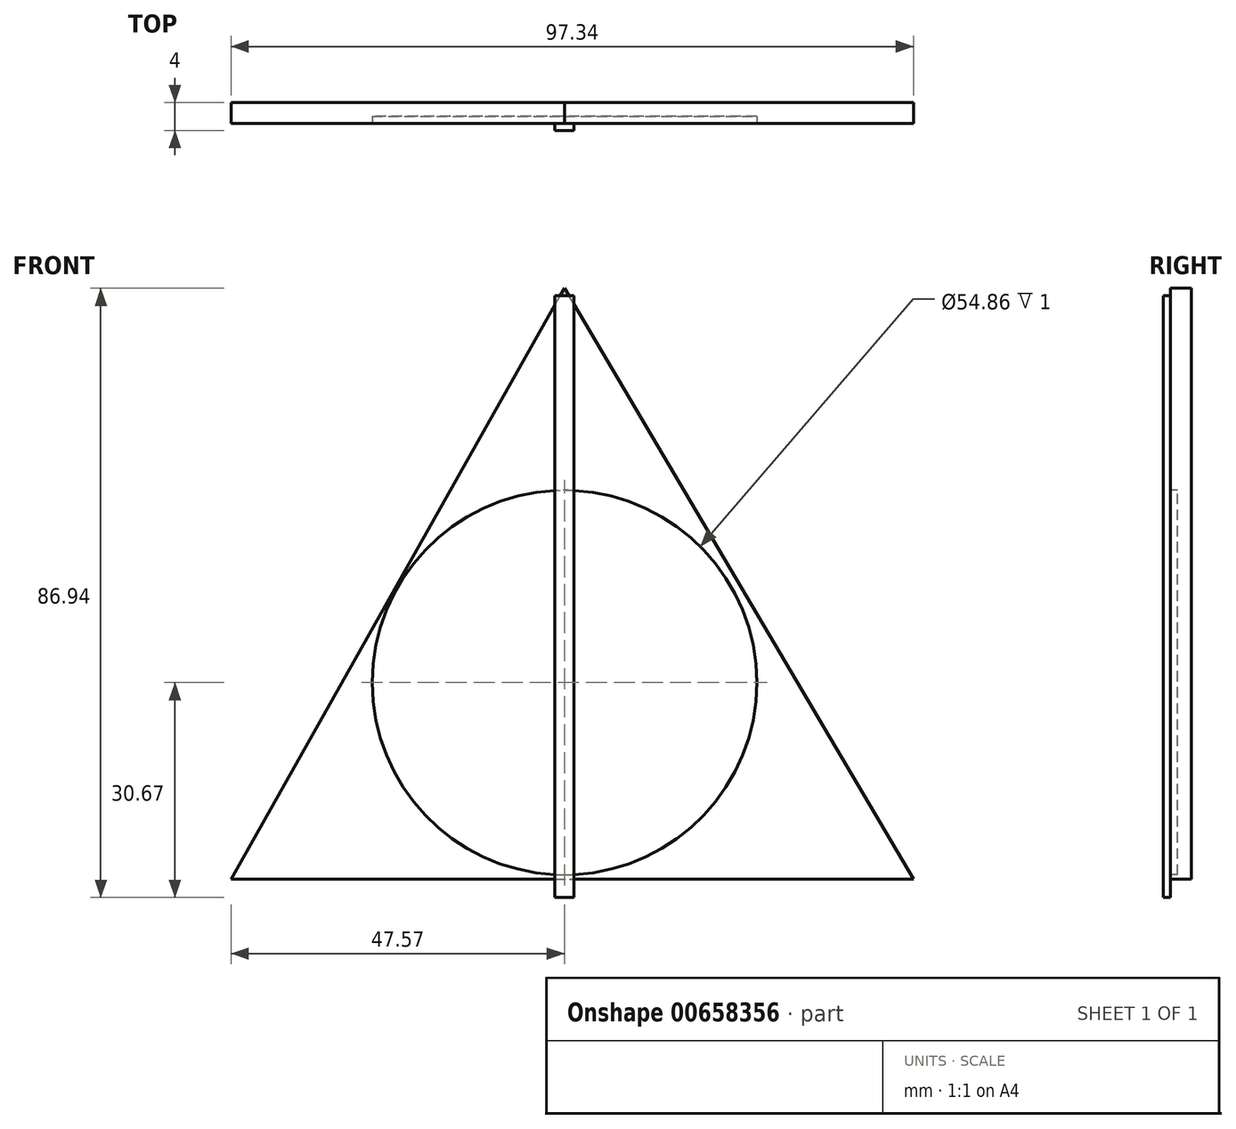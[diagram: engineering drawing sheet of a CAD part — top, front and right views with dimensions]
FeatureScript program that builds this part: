
annotation { "Feature Type Name" : "Feature", "Feature Type Description" : "" }
export const myFeature = defineFeature(function(context is Context, id is Id, definition is map)
    precondition{}
    {
        {
            var Q0;
            Q0=qCreatedBy(makeId("Front.planeOp"),FACE);
            var sketch = newSketch(context, id + "F0", { "sketchPlane" : qUnion([Q0])});
            skLineSegment(sketch, "E0", {"start": v(-47.57, -28.04) * mm, "end": v(49.77, -28.04) * mm});
            skLineSegment(sketch, "E1", {"start": v(-47.57, -28.04) * mm, "end": v(0, 56.27) * mm});
            skLineSegment(sketch, "E2", {"start": v(49.77, -28.04) * mm, "end": v(0, 56.27) * mm});
            skSolve(sketch);
        }
        {
            var Q0;
            Q0 = qSketchRegion(id + "F0", true);
            extrude(context, id + "F1", {"entities" : qUnion([Q0]), "depth" : 3 * mm, "offsetDistance" : 25.4 * mm});
        }
        {
            var Q0;
            Q0=makeQuery(id+"F1.opExtrude","CAP_FACE",FACE,{"disambiguationData":[OSD([sQuery(id+"F0.wireOp",EDGE,"E0"),sQuery(id+"F0.wireOp",EDGE,"E1"),sQuery(id+"F0.wireOp",EDGE,"E2")])],"isStart":false});
            var sketch = newSketch(context, id + "F2", { "sketchPlane" : qUnion([Q0])});
            skCircle(sketch, "E3", {"center": v(0, 0) * mm, "radius": 27.43 * mm});
            skSolve(sketch);
        }
        {
            var Q0;
            Q0 = qSketchRegion(id + "F2", true);
            extrude(context, id + "F3", {"entities" : qUnion([Q0]), "operationType" : NewBodyOperationType.REMOVE, "oppositeDirection" : true, "depth" : 1 * mm, "offsetDistance" : 25 * mm});
        }
        {
            var Q0;
            Q0=makeQuery(id+"F1.opExtrude","CAP_FACE",FACE,{"disambiguationData":[OSD([sQuery(id+"F0.wireOp",EDGE,"E0"),sQuery(id+"F0.wireOp",EDGE,"E1"),sQuery(id+"F0.wireOp",EDGE,"E2")])],"isStart":false});
            var sketch = newSketch(context, id + "F4", { "sketchPlane" : qUnion([Q0])});
            skLineSegment(sketch, "E4", {"start": v(0, 56.27) * mm, "end": v(0, -27.43) * mm});
            skSolve(sketch);
        }
        {
            var Q0;
            Q0=makeQuery(id+"F4.imprint","IMPRINT",FACE,{"disambiguationData":[TD([[makeQuery(id+"F4.imprint","IMPRINT",EDGE,{"derivedFrom":makeQuery(id+"F1.opExtrude","CAP_EDGE",EDGE,{"disambiguationData":[OSD([sQuery(id+"F0.wireOp",EDGE,"E0")])],"isStart":false})}),1.0]])]});
            var sketch = newSketch(context, id + "F5", { "sketchPlane" : qUnion([Q0])});
            skLineSegment(sketch, "E5.bottom", {"start": v(1.35, 55.2) * mm, "end": v(-1.35, 55.2) * mm});
            skLineSegment(sketch, "E5.top", {"start": v(1.35, -30.67) * mm, "end": v(-1.35, -30.67) * mm});
            skLineSegment(sketch, "E5.left", {"start": v(1.35, 55.2) * mm, "end": v(1.35, -30.67) * mm});
            skLineSegment(sketch, "E5.right", {"start": v(-1.35, 55.2) * mm, "end": v(-1.35, -30.67) * mm});
            skPoint(sketch, "E5.middle", {"position": v(0, 12.27) * mm});
            skSolve(sketch);
        }
        {
            var Q0;
            Q0 = qSketchRegion(id + "F5", true);
            extrude(context, id + "F6", {"entities" : qUnion([Q0]), "operationType" : NewBodyOperationType.ADD, "depth" : 1 * mm, "offsetDistance" : 25 * mm});
        }
    });
